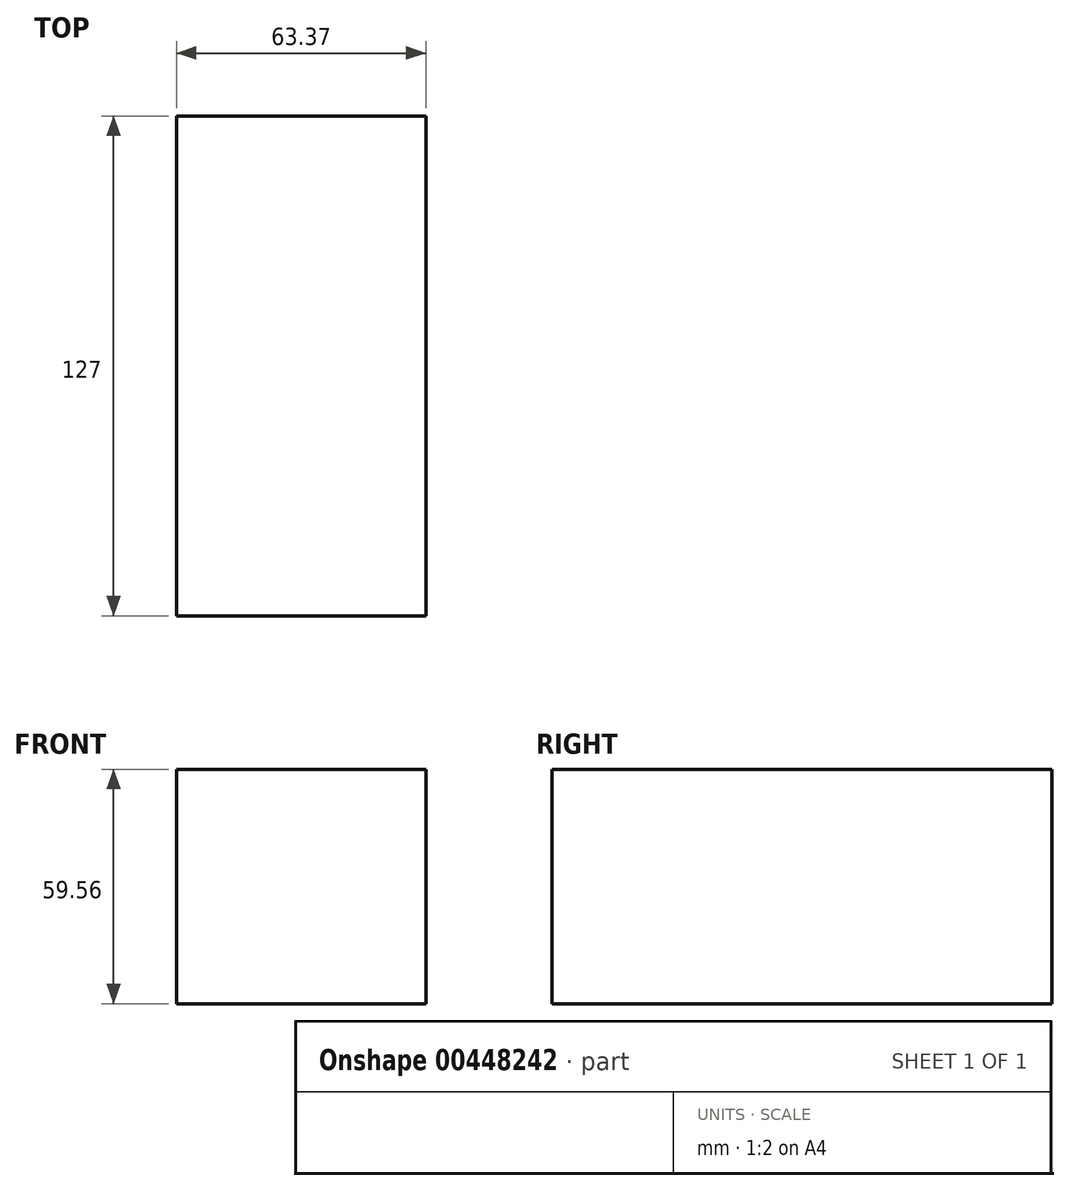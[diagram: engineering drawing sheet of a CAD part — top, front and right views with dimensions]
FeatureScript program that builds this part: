
annotation { "Feature Type Name" : "Feature", "Feature Type Description" : "" }
export const myFeature = defineFeature(function(context is Context, id is Id, definition is map)
    precondition{}
    {
        {
            var Q0;
            Q0=qCreatedBy(makeId("Front.planeOp"),FACE);
            var sketch = newSketch(context, id + "F0", { "sketchPlane" : qUnion([Q0])});
            skLineSegment(sketch, "E0.bottom", {"start": v(0, 4.77) * mm, "end": v(-63.37, 4.77) * mm});
            skLineSegment(sketch, "E0.top", {"start": v(0, 64.33) * mm, "end": v(-63.37, 64.33) * mm});
            skLineSegment(sketch, "E0.left", {"start": v(0, 4.77) * mm, "end": v(0, 64.33) * mm});
            skLineSegment(sketch, "E0.right", {"start": v(-63.37, 4.77) * mm, "end": v(-63.37, 64.33) * mm});
            skSolve(sketch);
        }
        {
            var Q0;
            Q0=makeQuery(id+"F0.imprint","IMPRINT",FACE,{"disambiguationData":[TD([[makeQuery(id+"F0.imprint","IMPRINT",EDGE,{"derivedFrom":sQuery(id+"F0.wireOp",EDGE,"E0.bottom")}),-1.0]])]});
            extrude(context, id + "F1", {"entities" : qUnion([Q0]), "depth" : 127 * mm});
        }
    });
